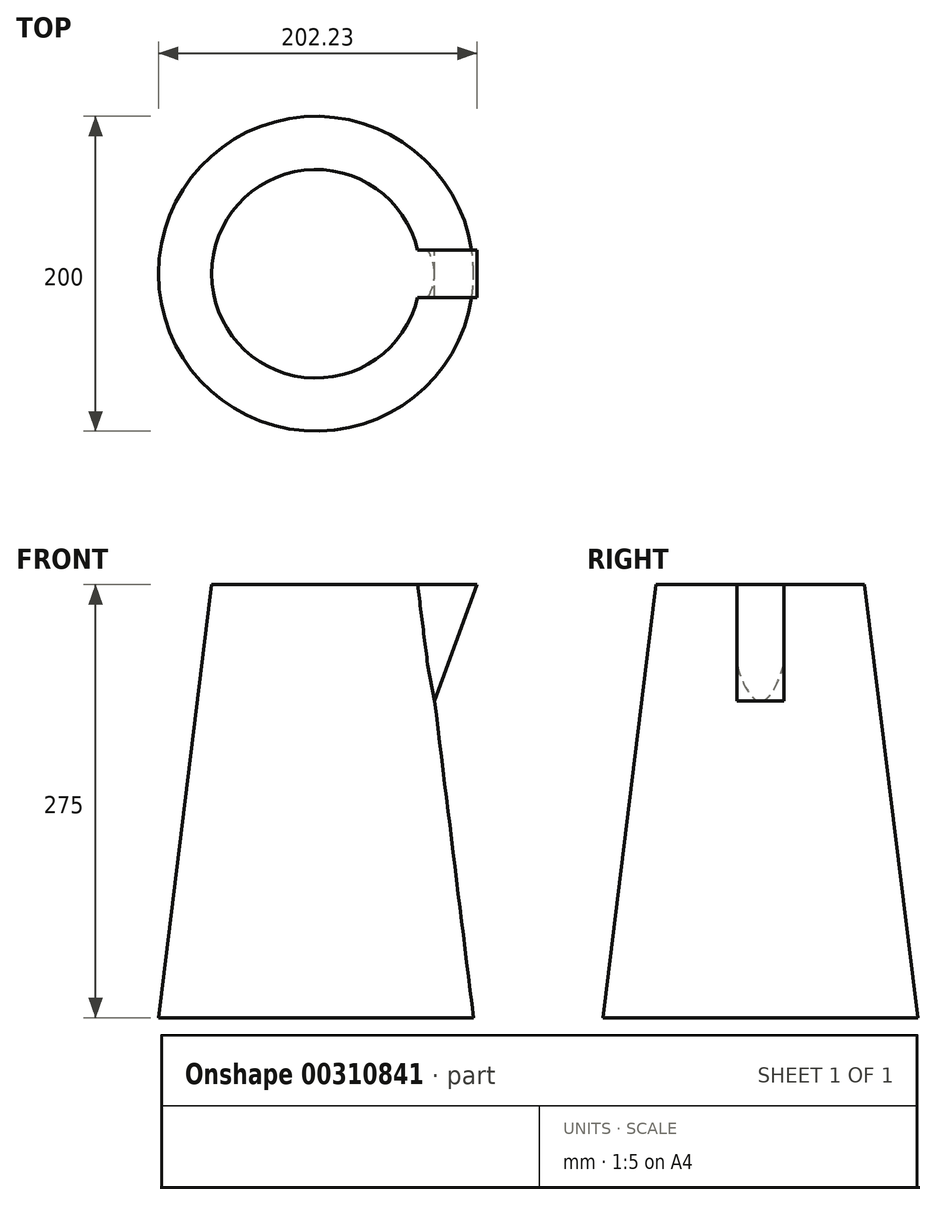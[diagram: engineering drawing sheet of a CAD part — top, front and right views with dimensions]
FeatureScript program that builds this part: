
annotation { "Feature Type Name" : "Feature", "Feature Type Description" : "" }
export const myFeature = defineFeature(function(context is Context, id is Id, definition is map)
    precondition{}
    {
        {
            var Q0;
            Q0=qCreatedBy(makeId("Top.planeOp"),FACE);
            var sketch = newSketch(context, id + "F0", { "sketchPlane" : qUnion([Q0])});
            skCircle(sketch, "E0", {"center": v(0, 0) * mm, "radius": 100 * mm});
            skSolve(sketch);
        }
        {
            var Q0;
            Q0=makeQuery(id+"F0.imprint","IMPRINT",FACE,{"disambiguationData":[TD([[makeQuery(id+"F0.imprint","IMPRINT",EDGE,{"derivedFrom":sQuery(id+"F0.wireOp",EDGE,"E0")}),1.0]])]});
            extrude(context, id + "F1", {"entities" : qUnion([Q0]), "depth" : 275 * mm, "hasDraft" : true, "draftAngle" : 7 * degree, "draftPullDirection" : true});
        }
        {
            var Q0;
            Q0=qCreatedBy(makeId("Front.planeOp"),FACE);
            var sketch = newSketch(context, id + "F2", { "sketchPlane" : qUnion([Q0])});
            skLineSegment(sketch, "E1.0.0", {"start": v(-66.23, 275) * mm, "end": v(66.23, 275) * mm});
            skLineSegment(sketch, "E2", {"start": v(66.23, 275) * mm, "end": v(102.23, 275) * mm});
            skLineSegment(sketch, "E3", {"start": v(-100, 0) * mm, "end": v(-66.23, 275) * mm});
            skLineSegment(sketch, "E4", {"start": v(66.23, 275) * mm, "end": v(100, 0) * mm});
            skLineSegment(sketch, "E5", {"start": v(102.23, 275) * mm, "end": v(75.32, 201.04) * mm});
            skLineSegment(sketch, "E6", {"start": v(66.23, 275) * mm, "end": v(61.23, 275) * mm});
            skLineSegment(sketch, "E7", {"start": v(61.23, 275) * mm, "end": v(75.32, 201.04) * mm});
            skSolve(sketch);
        }
        {
            var Q0;
            Q0 = qSketchRegion(id + "F2", true);
            extrude(context, id + "F3", {"entities" : qUnion([Q0]), "operationType" : NewBodyOperationType.ADD, "endBound" : BoundingType.SYMMETRIC, "depth" : 30 * mm});
        }
    });
